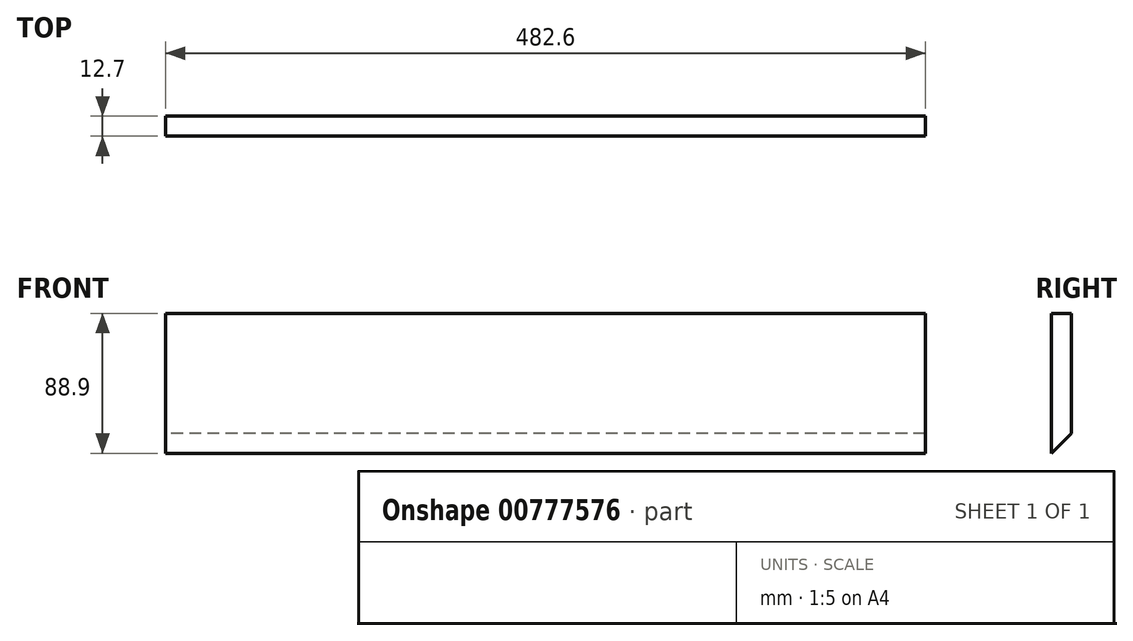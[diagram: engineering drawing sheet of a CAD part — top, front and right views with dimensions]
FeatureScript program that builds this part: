
annotation { "Feature Type Name" : "Feature", "Feature Type Description" : "" }
export const myFeature = defineFeature(function(context is Context, id is Id, definition is map)
    precondition{}
    {
        {
            var Q0;
            Q0=qCreatedBy(makeId("Right.planeOp"),FACE);
            var sketch = newSketch(context, id + "F0", { "sketchPlane" : qUnion([Q0])});
            skLineSegment(sketch, "E0", {"start": v(-6.88, 81.95) * mm, "end": v(5.82, 81.95) * mm});
            skLineSegment(sketch, "E1", {"start": v(5.82, 81.95) * mm, "end": v(5.82, 5.75) * mm});
            skLineSegment(sketch, "E2", {"start": v(5.82, 5.75) * mm, "end": v(-6.88, -6.95) * mm});
            skLineSegment(sketch, "E3", {"start": v(-6.88, -6.95) * mm, "end": v(-6.88, 81.95) * mm});
            skSolve(sketch);
        }
        {
            var Q0;
            Q0=makeQuery(id+"F0.imprint","IMPRINT",FACE,{"disambiguationData":[TD([[makeQuery(id+"F0.imprint","IMPRINT",EDGE,{"derivedFrom":sQuery(id+"F0.wireOp",EDGE,"E0")}),-1.0]])]});
            extrude(context, id + "F1", {"entities" : qUnion([Q0]), "depth" : 482.6 * mm, "offsetDistance" : 25.4 * mm});
        }
    });
